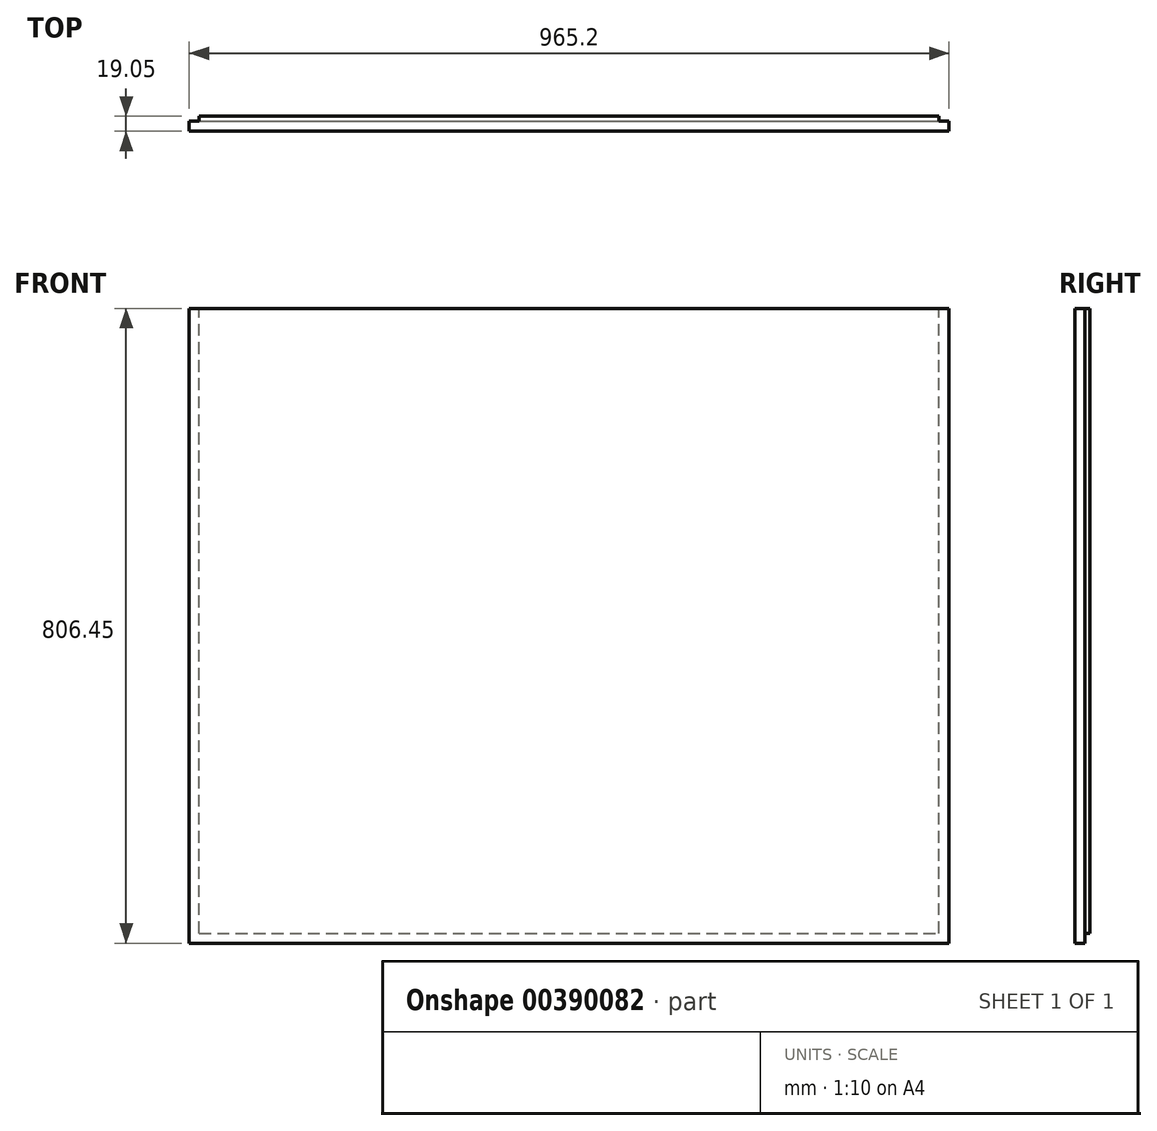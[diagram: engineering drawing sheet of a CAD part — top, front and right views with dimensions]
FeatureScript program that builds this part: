
annotation { "Feature Type Name" : "Feature", "Feature Type Description" : "" }
export const myFeature = defineFeature(function(context is Context, id is Id, definition is map)
    precondition{}
    {
        {
            var Q0;
            Q0=qCreatedBy(makeId("Front.planeOp"),FACE);
            var sketch = newSketch(context, id + "F0", { "sketchPlane" : qUnion([Q0])});
            skLineSegment(sketch, "E0", {"start": v(0, 0) * mm, "end": v(965.2, 0) * mm});
            skLineSegment(sketch, "E1", {"start": v(0, 0) * mm, "end": v(0, 806.45) * mm});
            skLineSegment(sketch, "E2", {"start": v(0, 806.45) * mm, "end": v(965.2, 806.45) * mm});
            skLineSegment(sketch, "E3", {"start": v(965.2, 806.45) * mm, "end": v(965.2, 0) * mm});
            skSolve(sketch);
        }
        {
            var Q0;
            Q0 = qSketchRegion(id + "F0", true);
            extrude(context, id + "F1", {"entities" : qUnion([Q0]), "depth" : 19.05 * mm});
        }
        {
            var Q0;
            Q0=makeQuery(id+"F1.opExtrude","SWEPT_FACE",FACE,{"disambiguationData":[OSD([sQuery(id+"F0.wireOp",EDGE,"E2")])]});
            var sketch = newSketch(context, id + "F2", { "sketchPlane" : qUnion([Q0])});
            skLineSegment(sketch, "E4", {"start": v(0, 0) * mm, "end": v(0, -6.35) * mm});
            skLineSegment(sketch, "E5", {"start": v(0, -6.35) * mm, "end": v(12.7, -6.35) * mm});
            skLineSegment(sketch, "E6", {"start": v(12.7, -6.35) * mm, "end": v(12.7, 0) * mm});
            skLineSegment(sketch, "E7", {"start": v(12.7, 0) * mm, "end": v(0, 0) * mm});
            skLineSegment(sketch, "E8", {"start": v(965.2, 0) * mm, "end": v(952.5, 0) * mm});
            skLineSegment(sketch, "E9", {"start": v(952.5, 0) * mm, "end": v(952.5, -6.35) * mm});
            skLineSegment(sketch, "E10", {"start": v(952.5, -6.35) * mm, "end": v(965.2, -6.35) * mm});
            skLineSegment(sketch, "E11", {"start": v(965.2, -6.35) * mm, "end": v(965.2, 0) * mm});
            skSolve(sketch);
        }
        {
            var Q0;
            Q0 = qSketchRegion(id + "F2", true);
            extrude(context, id + "F3", {"entities" : qUnion([Q0]), "operationType" : NewBodyOperationType.REMOVE, "endBound" : BoundingType.THROUGH_ALL, "oppositeDirection" : true, "depth" : 25.4 * mm});
        }
        {
            var Q0;
            Q0=makeQuery(id+"F1.opExtrude","SWEPT_FACE",FACE,{"disambiguationData":[OSD([sQuery(id+"F0.wireOp",EDGE,"E3")])]});
            var sketch = newSketch(context, id + "F4", { "sketchPlane" : qUnion([Q0])});
            skLineSegment(sketch, "E12", {"start": v(0, 0) * mm, "end": v(-6.35, 0) * mm});
            skLineSegment(sketch, "E13", {"start": v(-6.35, 0) * mm, "end": v(-6.35, 12.7) * mm});
            skLineSegment(sketch, "E14", {"start": v(-6.35, 12.7) * mm, "end": v(0, 12.7) * mm});
            skLineSegment(sketch, "E15", {"start": v(0, 12.7) * mm, "end": v(0, 0) * mm});
            skSolve(sketch);
        }
        {
            var Q0;
            Q0 = qSketchRegion(id + "F4", true);
            extrude(context, id + "F5", {"entities" : qUnion([Q0]), "operationType" : NewBodyOperationType.REMOVE, "endBound" : BoundingType.THROUGH_ALL, "oppositeDirection" : true, "depth" : 25.4 * mm});
        }
    });
